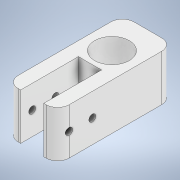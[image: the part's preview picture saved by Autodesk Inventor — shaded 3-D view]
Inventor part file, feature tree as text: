
AUTODESK INVENTOR PART (.ipt)
format: ipt  version: 2022 (Build 260153000, 153)  size: 309,760 bytes
history: native  units: mm
features: sketch x4, extrude x2, hole x2, other x1, fillet x1
ambient origin geometry x8: Origin, YZ Plane, XZ Plane, XY Plane, X Axis, Y Axis, Z Axis, Center Point
bodies: Body1 (feature_tree)
feature tree (10):
  other  "Sólido1"
  extrude  "Extrusão1"  Depth=20.0mm
  hole  "Furo1"  [1 undecoded]
  fillet  "Arredondamento1"  Radius=11.0mm
  extrude  "Extrusão2"  Depth=10.0mm
  hole  "Furo3"  [1 undecoded]
  sketch  "Esboço1"  dims[d0=22.0mm d1=20.0mm]
  sketch  "Esboço2"  dims[d2=50.0mm d3=0.0mm]
  sketch  "Esboço4"  dims[d4=15.0mm d5=6.0mm d6=4.0mm d7=2.0mm d8=90.0deg d9=8.0mm d10=20.594885mm d18=5.0mm d20=11.0mm]
  sketch  "Esboço5"  dims[d22=25.0mm d23=10.0mm d24=0.0mm d25=0.0mm d26=3.0mm d27=6.0mm d28=4.0mm d29=2.0mm d30=90.0deg d31=8.0mm d32=20.594885mm d33=5.0mm d34=10.0mm d35=34.49725mm]
note: 2 required parameter values undecoded (feature->parameter linkage not recoverable at this tier; creation-order binding heuristic only, values carry confidence <= 0.55)
